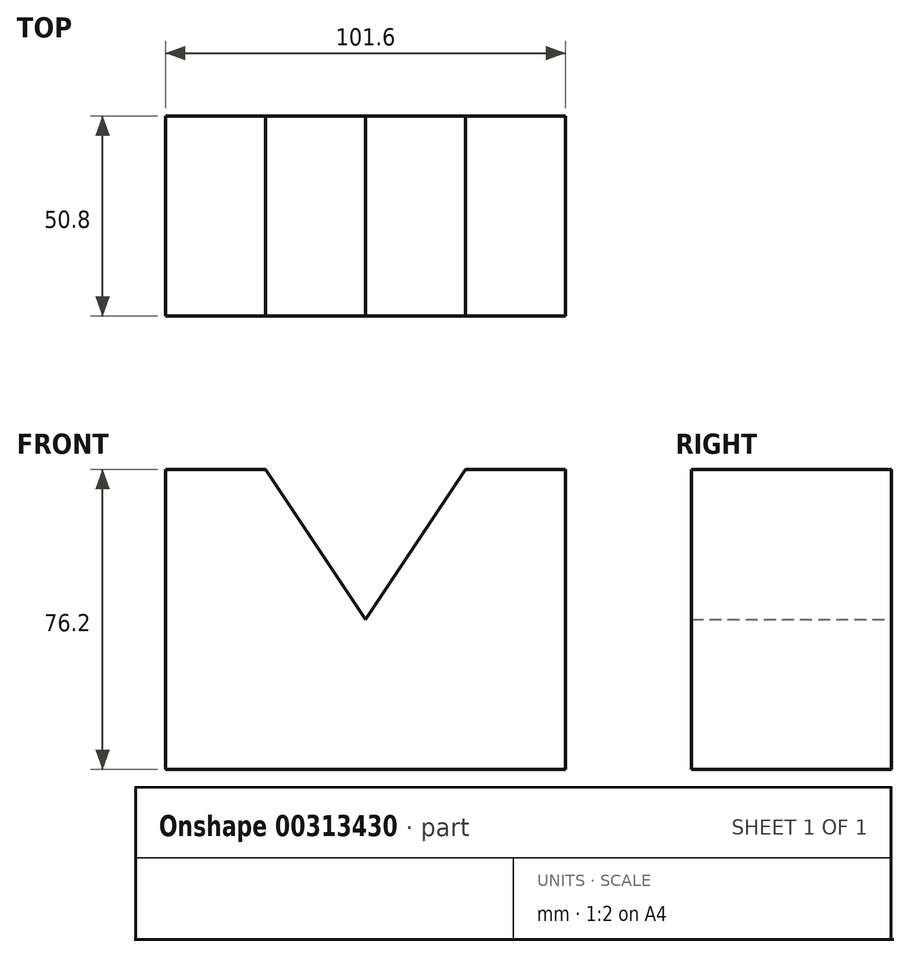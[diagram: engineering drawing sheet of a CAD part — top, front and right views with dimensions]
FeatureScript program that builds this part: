
annotation { "Feature Type Name" : "Feature", "Feature Type Description" : "" }
export const myFeature = defineFeature(function(context is Context, id is Id, definition is map)
    precondition{}
    {
        {
            var Q0;
            Q0=qCreatedBy(makeId("Front.planeOp"),FACE);
            var sketch = newSketch(context, id + "F0", { "sketchPlane" : qUnion([Q0])});
            skLineSegment(sketch, "E0", {"start": v(-51.34, -15.26) * mm, "end": v(50.26, -15.26) * mm});
            skLineSegment(sketch, "E1", {"start": v(50.26, -15.26) * mm, "end": v(50.26, 60.94) * mm});
            skLineSegment(sketch, "E2", {"start": v(50.26, 60.94) * mm, "end": v(24.86, 60.94) * mm});
            skLineSegment(sketch, "E3", {"start": v(-51.34, -15.26) * mm, "end": v(-51.34, 60.94) * mm});
            skLineSegment(sketch, "E4", {"start": v(-51.34, 60.94) * mm, "end": v(-25.94, 60.94) * mm});
            skPoint(sketch, "E5.endSnap0", {"position": v(-51.34, 22.84) * mm});
            skLineSegment(sketch, "E6", {"start": v(-0.54, 22.84) * mm, "end": v(-25.94, 60.94) * mm});
            skLineSegment(sketch, "E7", {"start": v(-0.54, 22.84) * mm, "end": v(24.86, 60.94) * mm});
            skSolve(sketch);
        }
        {
            var Q0;
            Q0 = qSketchRegion(id + "F0", true);
            extrude(context, id + "F1", {"entities" : qUnion([Q0]), "depth" : 50.8 * mm});
        }
    });
